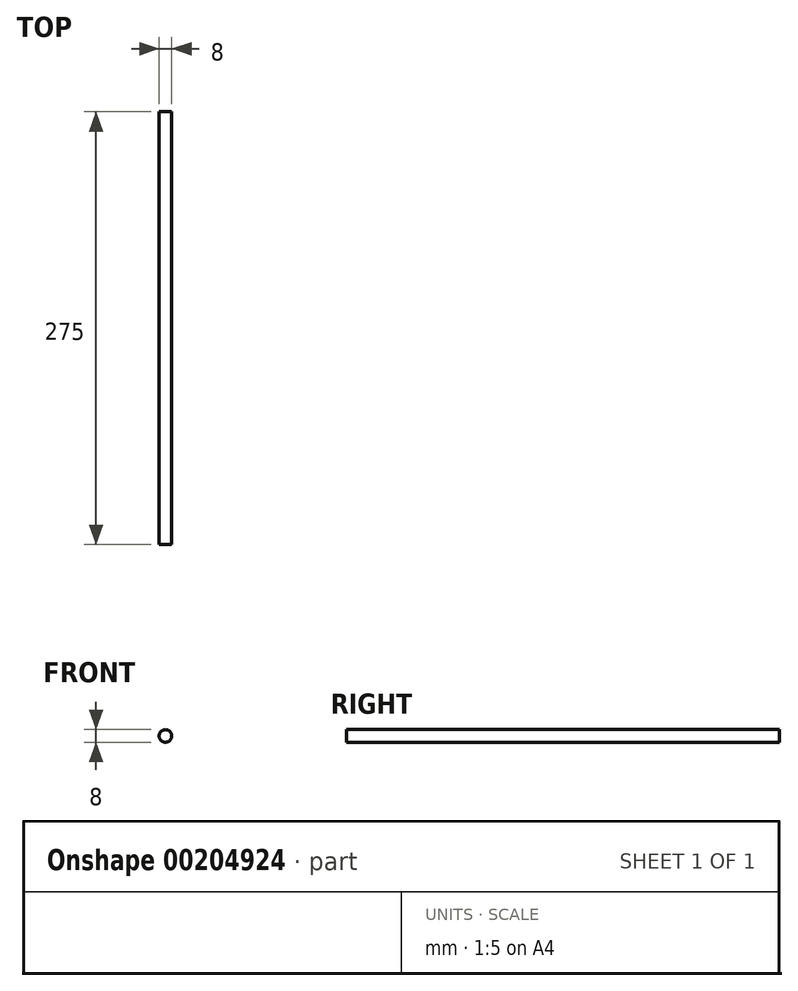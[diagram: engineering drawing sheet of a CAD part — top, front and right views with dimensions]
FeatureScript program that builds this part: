
annotation { "Feature Type Name" : "Feature", "Feature Type Description" : "" }
export const myFeature = defineFeature(function(context is Context, id is Id, definition is map)
    precondition{}
    {
        {
            var Q0;
            Q0=qCreatedBy(makeId("Front.planeOp"),FACE);
            var sketch = newSketch(context, id + "F0", { "sketchPlane" : qUnion([Q0])});
            skCircle(sketch, "E0", {"center": v(0, 0) * mm, "radius": 4 * mm});
            skSolve(sketch);
        }
        {
            var Q0;
            Q0=makeQuery(id+"F0.imprint","IMPRINT",FACE,{"disambiguationData":[TD([[makeQuery(id+"F0.imprint","IMPRINT",EDGE,{"derivedFrom":sQuery(id+"F0.wireOp",EDGE,"E0")}),1.0]])]});
            extrude(context, id + "F1", {"entities" : qUnion([Q0]), "depth" : 400 * mm});
        }
        {
            var Q0;
            Q0=makeQuery(id+"F1.opExtrude","CAP_FACE",FACE,{"disambiguationData":[OSD([sQuery(id+"F0.wireOp",EDGE,"E0")])],"isStart":false});
            extrude(context, id + "F2", {"entities" : qUnion([Q0]), "operationType" : NewBodyOperationType.REMOVE, "oppositeDirection" : true, "depth" : 100 * mm});
        }
        {
            var Q0;
            Q0=makeQuery(id+"F2.boolean.opBoolean","COPY",FACE,{"derivedFrom":makeQuery(id+"F2.opExtrude","CAP_FACE",FACE,{"disambiguationData":[OSD([sQuery(id+"F0.wireOp",EDGE,"E0")])],"isStart":false})});
            extrude(context, id + "F3", {"entities" : qUnion([Q0]), "operationType" : NewBodyOperationType.REMOVE, "oppositeDirection" : true, "depth" : 25 * mm});
        }
    });
